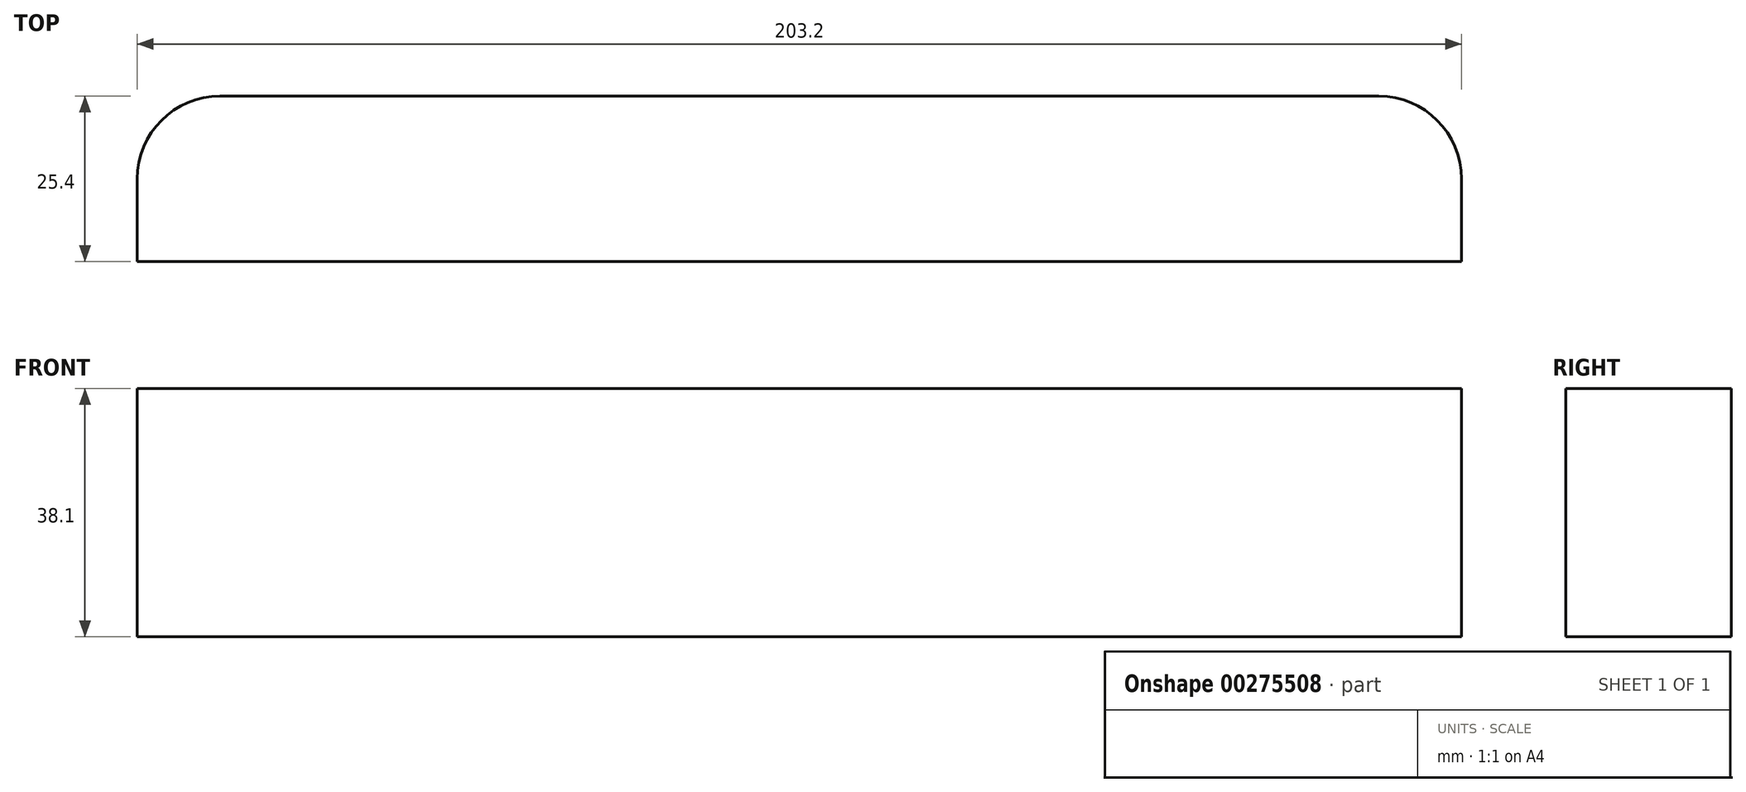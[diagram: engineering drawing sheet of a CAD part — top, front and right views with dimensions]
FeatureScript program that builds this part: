
annotation { "Feature Type Name" : "Feature", "Feature Type Description" : "" }
export const myFeature = defineFeature(function(context is Context, id is Id, definition is map)
    precondition{}
    {
        {
            var Q0;
            Q0=qCreatedBy(makeId("Top.planeOp"),FACE);
            var sketch = newSketch(context, id + "F0", { "sketchPlane" : qUnion([Q0])});
            skLineSegment(sketch, "E0.bottom", {"start": v(-80.27, 58.74) * mm, "end": v(97.53, 58.74) * mm});
            skLineSegment(sketch, "E0.top", {"start": v(-92.97, 33.34) * mm, "end": v(110.23, 33.34) * mm});
            skLineSegment(sketch, "E0.left", {"start": v(-92.97, 46.04) * mm, "end": v(-92.97, 33.34) * mm});
            skLineSegment(sketch, "E0.right", {"start": v(110.23, 46.04) * mm, "end": v(110.23, 33.34) * mm});
            skLineSegment(sketch, "E1.bottom", {"start": v(-92.97, 33.34) * mm, "end": v(-57.4, 33.34) * mm});
            skLineSegment(sketch, "E1.top", {"start": v(-92.97, -42.86) * mm, "end": v(-57.4, -42.86) * mm});
            skLineSegment(sketch, "E1.left", {"start": v(-92.97, 33.34) * mm, "end": v(-92.97, -42.86) * mm});
            skLineSegment(sketch, "E1.right", {"start": v(-57.4, 33.34) * mm, "end": v(-57.4, -42.86) * mm});
            skLineSegment(sketch, "E2.bottom", {"start": v(110.23, 33.34) * mm, "end": v(74.67, 33.34) * mm});
            skLineSegment(sketch, "E2.top", {"start": v(110.23, -42.86) * mm, "end": v(74.67, -42.86) * mm});
            skLineSegment(sketch, "E2.left", {"start": v(110.23, 33.34) * mm, "end": v(110.23, -42.86) * mm});
            skLineSegment(sketch, "E2.right", {"start": v(74.67, 33.34) * mm, "end": v(74.67, -42.86) * mm});
            skPoint(sketch, "E3.visualSharp", {"position": v(-92.97, 58.74) * mm});
            skArc(sketch, "E3.filletArc", {"start": v(-80.27, 58.74) * mm, "mid": v(-89.25, 55.02) * mm, "end": v(-92.97, 46.04) * mm});
            skPoint(sketch, "E4.visualSharp", {"position": v(110.23, 58.74) * mm});
            skArc(sketch, "E4.filletArc", {"start": v(110.23, 46.04) * mm, "mid": v(106.51, 55.02) * mm, "end": v(97.53, 58.74) * mm});
            skSolve(sketch);
        }
        {
            var Q0;
            Q0=makeQuery(id+"F0.imprint","IMPRINT",FACE,{"disambiguationData":[TD([[makeQuery(id+"F0.imprint","IMPRINT",EDGE,{"derivedFrom":sQuery(id+"F0.wireOp",EDGE,"E0.bottom")}),-1.0]])]});
            var Q1;
            Q1=makeQuery(id+"F0.imprint","IMPRINT",FACE,{"disambiguationData":[TD([[makeQuery(id+"F0.imprint","IMPRINT",EDGE,{"derivedFrom":sQuery(id+"F0.wireOp",EDGE,"E1.bottom")}),-1.0]])]});
            var Q2;
            Q2=makeQuery(id+"F0.imprint","IMPRINT",FACE,{"disambiguationData":[TD([[makeQuery(id+"F0.imprint","IMPRINT",EDGE,{"derivedFrom":sQuery(id+"F0.wireOp",EDGE,"E2.bottom")}),1.0]])]});
            extrude(context, id + "F1", {"entities" : qUnion([Q0, Q1, Q2]), "depth" : 38.1 * mm});
        }
        {
            var Q0;
            Q0=makeQuery(id+"F1.opExtrude","CAP_FACE",FACE,{"disambiguationData":[OSD([sQuery(id+"F0.wireOp",EDGE,"E0.bottom"),sQuery(id+"F0.wireOp",EDGE,"E0.top"),sQuery(id+"F0.wireOp",EDGE,"E0.left"),sQuery(id+"F0.wireOp",EDGE,"E0.right"),sQuery(id+"F0.wireOp",EDGE,"E1.top"),sQuery(id+"F0.wireOp",EDGE,"E1.left"),sQuery(id+"F0.wireOp",EDGE,"E1.right"),sQuery(id+"F0.wireOp",EDGE,"E2.top"),sQuery(id+"F0.wireOp",EDGE,"E2.left"),sQuery(id+"F0.wireOp",EDGE,"E2.right"),sQuery(id+"F0.wireOp",EDGE,"E3.filletArc"),sQuery(id+"F0.wireOp",EDGE,"E4.filletArc")])],"isStart":false});
            var sketch = newSketch(context, id + "F2", { "sketchPlane" : qUnion([Q0])});
            skCircle(sketch, "E5", {"center": v(-75.5, -19.05) * mm, "radius": 4.76 * mm});
            skCircle(sketch, "E6", {"center": v(92.77, -19.05) * mm, "radius": 4.76 * mm});
            skSolve(sketch);
        }
        {
            var Q0;
            Q0=sQuery(id+"F2.wireOp",VERTEX,"E5.center");
            var Q1;
            Q1=sQuery(id+"F2.wireOp",VERTEX,"E6.center");
            var Q2;
            Q2=makeQuery(id+"F1.opExtrude","SWEPT_BODY",BODY,{"disambiguationData":[OSD([sQuery(id+"F0.wireOp",EDGE,"E0.bottom"),sQuery(id+"F0.wireOp",EDGE,"E0.top"),sQuery(id+"F0.wireOp",EDGE,"E0.left"),sQuery(id+"F0.wireOp",EDGE,"E0.right"),sQuery(id+"F0.wireOp",EDGE,"E1.top"),sQuery(id+"F0.wireOp",EDGE,"E1.left"),sQuery(id+"F0.wireOp",EDGE,"E1.right"),sQuery(id+"F0.wireOp",EDGE,"E2.top"),sQuery(id+"F0.wireOp",EDGE,"E2.left"),sQuery(id+"F0.wireOp",EDGE,"E2.right"),sQuery(id+"F0.wireOp",EDGE,"E3.filletArc"),sQuery(id+"F0.wireOp",EDGE,"E4.filletArc")])]});
            hole(context, id + "F3", {"style" : HoleStyle.C_SINK, "endStyle" : HoleEndStyle.THROUGH, "standardTappedOrClearance" : lookupTablePath({ "standard" : "ANSI", "size" : "3/8 (0.38)", "type" : "Drilled" }), "standardBlindInLast" : lookupTablePath({ "standard" : "ANSI", "size" : "3/8", "type" : "Drilled" }), "holeDiameter" : 3 / 203.2 * mm, "cSinkDiameter" : 13.5 * mm, "cSinkAngle" : 82 * degree, "tappedDepth" : 12.7 * mm, "tapClearance" : 3, "locations" : qUnion([Q0, Q1]), "scope" : qUnion([Q2])});
        }
    });
